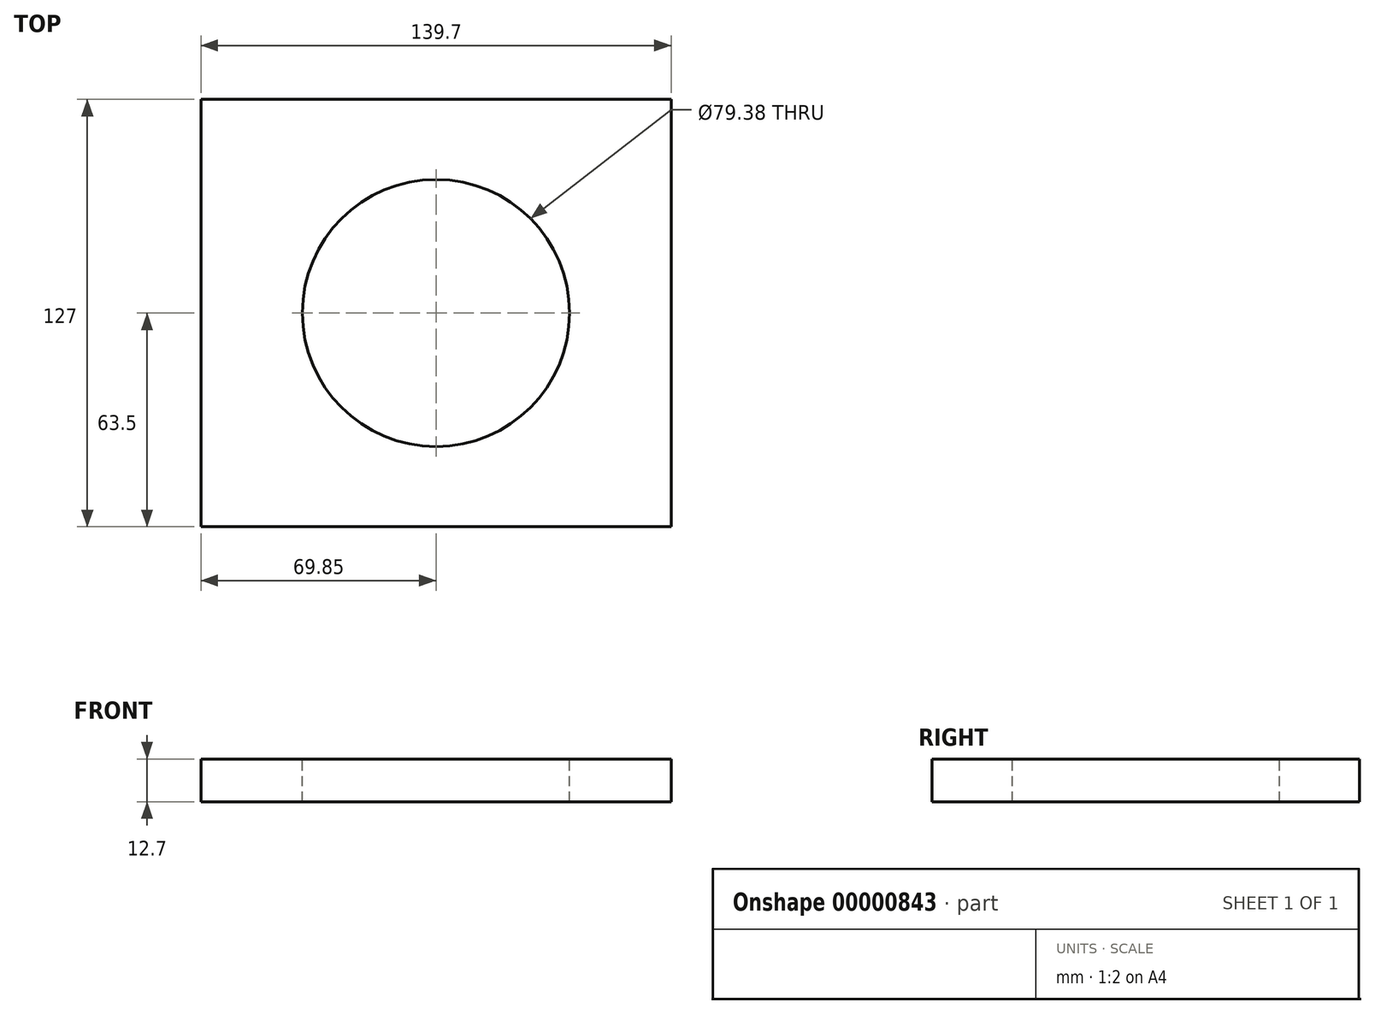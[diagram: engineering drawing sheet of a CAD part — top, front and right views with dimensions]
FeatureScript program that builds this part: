
annotation { "Feature Type Name" : "Feature", "Feature Type Description" : "" }
export const myFeature = defineFeature(function(context is Context, id is Id, definition is map)
    precondition{}
    {
        {
            var Q0;
            Q0=qCreatedBy(makeId("Top.planeOp"),FACE);
            var sketch = newSketch(context, id + "F0", { "sketchPlane" : qUnion([Q0])});
            skLineSegment(sketch, "E0.bottom", {"start": v(-69.85, 63.5) * mm, "end": v(69.85, 63.5) * mm});
            skLineSegment(sketch, "E0.top", {"start": v(-69.85, -63.5) * mm, "end": v(69.85, -63.5) * mm});
            skLineSegment(sketch, "E0.left", {"start": v(-69.85, 63.5) * mm, "end": v(-69.85, -63.5) * mm});
            skLineSegment(sketch, "E0.right", {"start": v(69.85, 63.5) * mm, "end": v(69.85, -63.5) * mm});
            skCircle(sketch, "E1", {"center": v(0, 0) * mm, "radius": 39.69 * mm});
            skLineSegment(sketch, "E2", {"start": v(-69.85, 63.5) * mm, "end": v(69.85, -63.5) * mm, "construction": true});
            skLineSegment(sketch, "E3", {"start": v(-69.85, -63.5) * mm, "end": v(69.85, 63.5) * mm, "construction": true});
            skSolve(sketch);
        }
        {
            var Q0;
            Q0=makeQuery(id+"F0.imprint","IMPRINT",FACE,{"disambiguationData":[TD([[makeQuery(id+"F0.imprint","IMPRINT",EDGE,{"derivedFrom":sQuery(id+"F0.wireOp",EDGE,"E0.bottom")}),-1.0]])]});
            extrude(context, id + "F1", {"entities" : qUnion([Q0]), "oppositeDirection" : true, "depth" : 12.7 * mm});
        }
    });
